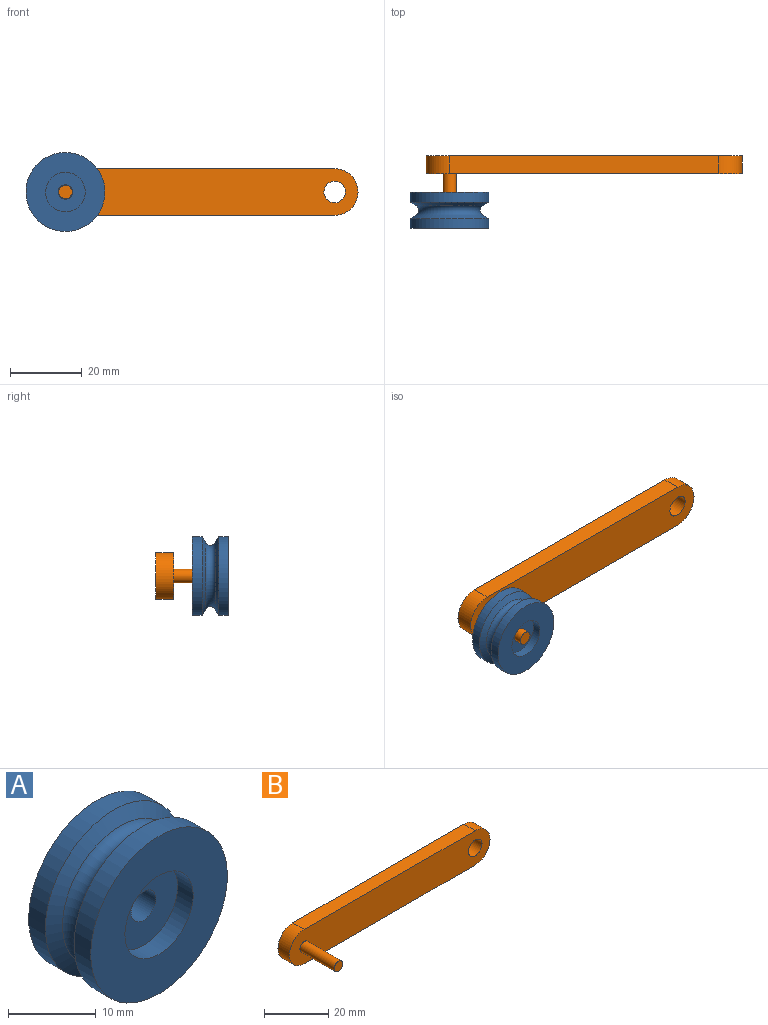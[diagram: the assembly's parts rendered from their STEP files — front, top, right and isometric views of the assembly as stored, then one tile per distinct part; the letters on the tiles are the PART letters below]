
ASSEMBLY  parts=2 mates=1
PART A: 12 faces, bbox 22x10x22 mm
  f0: cylinder r=2mm len=5mm, axis (0,-1,0), area 62.8mm2, adj f1,f11
  f1: plane 11x11mm, normal (0,1,0), area 82.5mm2, adj f0,f2
  f2: cylinder r=5.5mm len=11mm, axis (0,-1,0), area 86.4mm2, adj f1,f3
  f3: plane 22x22mm, normal (0,1,0), area 285.1mm2, adj f2,f4
  f4: cylinder r=11mm len=22mm, axis (0,-1,0), area 186mm2, adj f3,f5
  f5: cone r=11mm half-angle=60deg, axis (0,1,0), area 128.6mm2, adj f4,f6
  f6: torus R=10mm, axis (0,-1,0), area 172.9mm2, adj f5,f7
  f7: cone r=9.25mm half-angle=60deg, axis (0,-1,0), area 128.6mm2, adj f6,f8
  f8: cylinder r=11mm len=22mm, axis (0,-1,0), area 186mm2, adj f7,f9
  f9: plane 22x22mm, normal (0,-1,0), area 285.1mm2, adj f8,f10
  f10: cylinder r=5.5mm len=11mm, axis (0,-1,0), area 86.4mm2, adj f9,f11
  f11: plane 11x11mm, normal (0,-1,0), area 82.5mm2, adj f0,f10
PART B: 9 faces, bbox 88x20x13 mm
  f0: plane 75x5mm, normal (0,0,1), area 375mm2, adj f1,f4,f5,f6
  f1: cylinder r=6.5mm len=13mm, axis (0,1,0), area 102.1mm2, adj f0,f2,f5,f6
  f2: plane 75x5mm, normal (0,0,-1), area 375mm2, adj f1,f4,f5,f6
  f3: cylinder r=3mm len=6mm, axis (0,1,0), area 94.2mm2, adj f5,f6
  f4: cylinder r=6.5mm len=13mm, axis (0,1,0), area 102.1mm2, adj f0,f2,f5,f6
  f5: plane 88x13mm, normal (0,-1,0), area 1068.1mm2, adj f0,f1,f2,f3,f4,f7
  f6: plane 88x13mm, normal (0,1,0), area 1079.5mm2, adj f0,f1,f2,f3,f4
  f7: cylinder r=1.9mm len=15mm, axis (0,1,0), area 179.1mm2, adj f5,f8
  f8: plane 3.8x3.8mm, normal (0,-1,0), area 11.3mm2, adj f7
PLACE A rot(axis=(0,1,0),108.1deg) t=(6.65,-15.56,-39.46)mm
PLACE B t=(6.65,-0.31,-39.46)mm fixed
MATE cylindrical B.f7 <-> A.f0  axis (0,-1,0) through (6.65,-20.31,-39.46)mm
